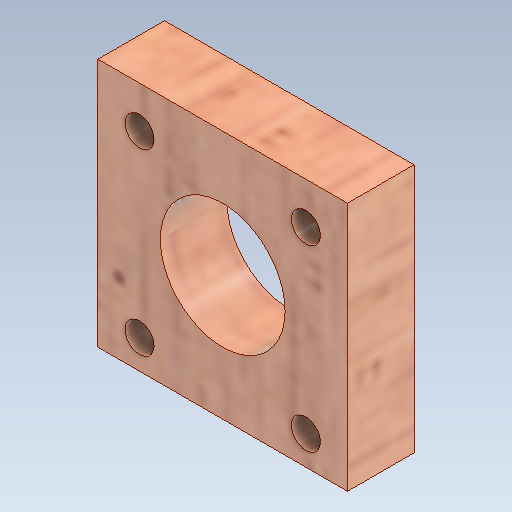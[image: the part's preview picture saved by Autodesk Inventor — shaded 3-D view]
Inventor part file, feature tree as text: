
AUTODESK INVENTOR PART (.ipt)
format: ipt  version: 2020 (Build 240168000, 168)  size: 238,080 bytes
history: native  units: mm
features: extrude x3, sketch x3
ambient origin geometry x8: Origin, YZ Plane, XZ Plane, XY Plane, X Axis, Y Axis, Z Axis, Center Point
bodies: Solid1 (feature_tree)
feature tree (6):
  extrude  "Extrusion1"  Depth=30.0mm
  extrude  "Extrusion2"  TaperAngle=0.0deg  [1 undecoded]
  extrude  "Extrusion3"  Depth=3.5mm
  sketch  "Sketch1"  dims[d0=30.0mm d1=30.0mm]
  sketch  "Sketch2"  dims[d2=8.0mm d3=0.0mm d6=0.0mm d7=0.0mm]
  sketch  "Sketch3"  dims[d9=3.5mm d10=3.5mm d12=5.0mm d13=5.0mm d14=5.0mm d15=0.0mm d16=0.0mm d17=15.0mm d18=3.5mm]
note: 1 required parameter value undecoded (feature->parameter linkage not recoverable at this tier; creation-order binding heuristic only, values carry confidence <= 0.55)
